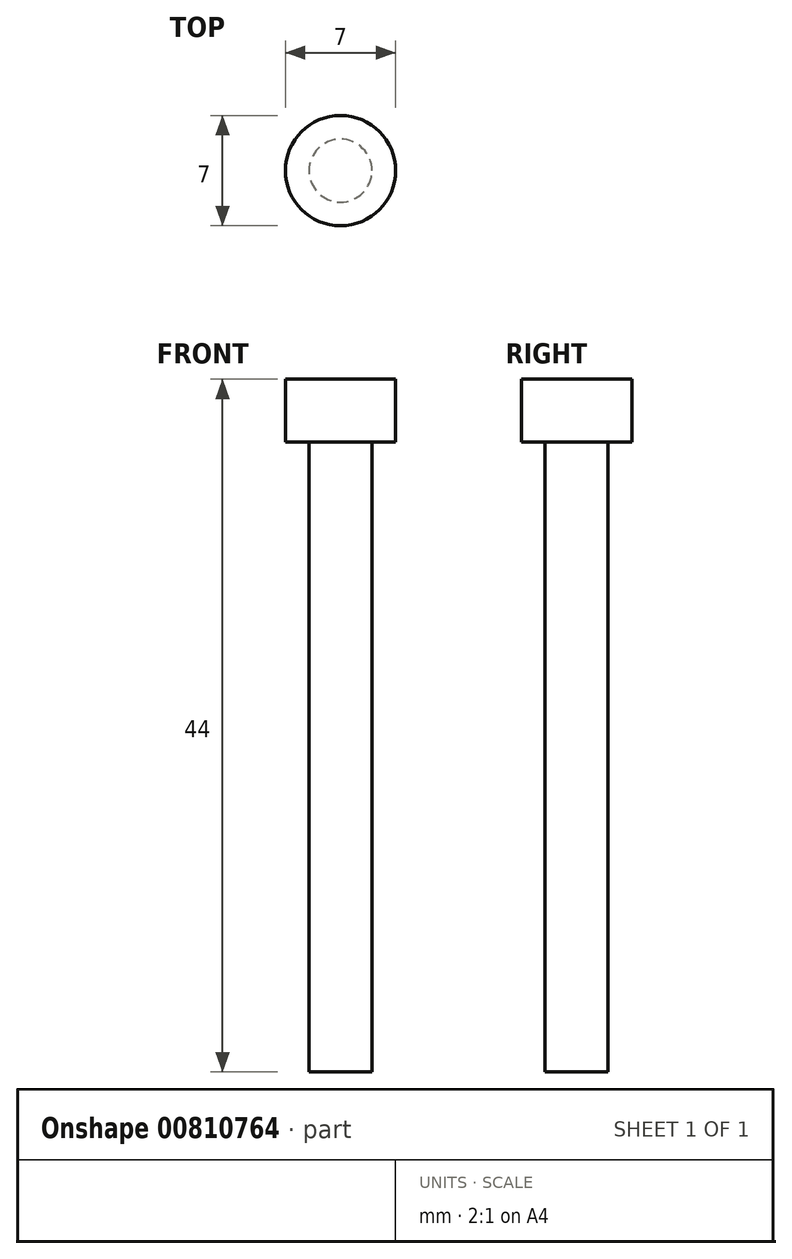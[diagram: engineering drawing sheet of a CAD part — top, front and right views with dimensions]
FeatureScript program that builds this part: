
annotation { "Feature Type Name" : "Feature", "Feature Type Description" : "" }
export const myFeature = defineFeature(function(context is Context, id is Id, definition is map)
    precondition{}
    {
        {
            var Q0;
            Q0=qCreatedBy(makeId("Top.planeOp"),FACE);
            var sketch = newSketch(context, id + "F0", { "sketchPlane" : qUnion([Q0])});
            skCircle(sketch, "E0", {"center": v(0, 0) * mm, "radius": 2 * mm});
            skSolve(sketch);
        }
        {
            var Q0;
            Q0=qSketchRegion(id+"F0",true);
            extrude(context, id + "F1", {"entities" : qUnion([Q0]), "oppositeDirection" : true, "depth" : 40 * mm});
        }
        {
            var Q0;
            Q0=qCreatedBy(makeId("Top.planeOp"),FACE);
            var sketch = newSketch(context, id + "F2", { "sketchPlane" : qUnion([Q0])});
            skCircle(sketch, "E1", {"center": v(0, 0) * mm, "radius": 3.5 * mm});
            skSolve(sketch);
        }
        {
            var Q0;
            Q0=qSketchRegion(id+"F2",true);
            extrude(context, id + "F3", {"entities" : qUnion([Q0]), "operationType" : NewBodyOperationType.ADD, "depth" : 4 * mm});
        }
    });
